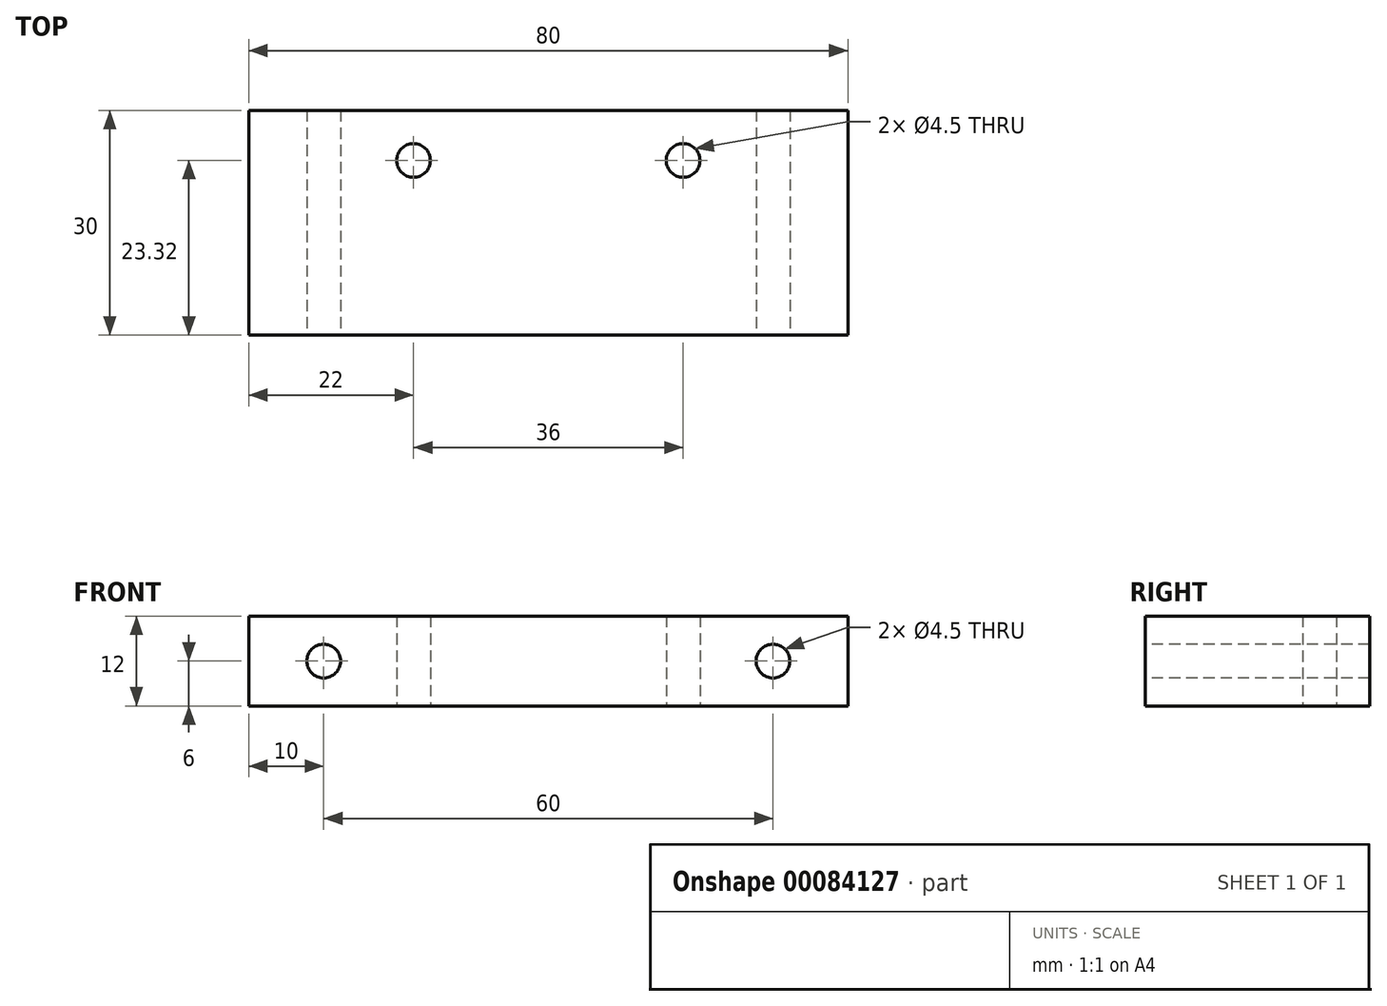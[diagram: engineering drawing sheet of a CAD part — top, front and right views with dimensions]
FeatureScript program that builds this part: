
annotation { "Feature Type Name" : "Feature", "Feature Type Description" : "" }
export const myFeature = defineFeature(function(context is Context, id is Id, definition is map)
    precondition{}
    {
        {
            var Q0;
            Q0=qCreatedBy(makeId("Top.planeOp"),FACE);
            var sketch = newSketch(context, id + "F0", { "sketchPlane" : qUnion([Q0])});
            skLineSegment(sketch, "E0.bottom", {"start": v(40, -15) * mm, "end": v(-40, -15) * mm});
            skLineSegment(sketch, "E0.top", {"start": v(40, 15) * mm, "end": v(-40, 15) * mm});
            skLineSegment(sketch, "E0.left", {"start": v(40, -15) * mm, "end": v(40, 15) * mm});
            skLineSegment(sketch, "E0.right", {"start": v(-40, -15) * mm, "end": v(-40, 15) * mm});
            skPoint(sketch, "E0.middle", {"position": v(0, 0) * mm});
            skLineSegment(sketch, "E1", {"start": v(-18, 8.32) * mm, "end": v(18, 8.32) * mm, "construction": true});
            skPoint(sketch, "E2", {"position": v(0, 8.32) * mm});
            skCircle(sketch, "E3", {"center": v(-18, 8.32) * mm, "radius": 2.25 * mm});
            skCircle(sketch, "E4", {"center": v(18, 8.32) * mm, "radius": 2.25 * mm});
            skSolve(sketch);
        }
        {
            var Q0;
            Q0=makeQuery(id+"F0.imprint","IMPRINT",FACE,{"disambiguationData":[TD([[makeQuery(id+"F0.imprint","IMPRINT",EDGE,{"derivedFrom":sQuery(id+"F0.wireOp",EDGE,"E0.bottom")}),-1.0]])]});
            extrude(context, id + "F1", {"entities" : qUnion([Q0]), "depth" : 12 * mm});
        }
        {
            var Q0;
            Q0=makeQuery(id+"F1.opExtrude","SWEPT_FACE",FACE,{"disambiguationData":[OSD([sQuery(id+"F0.wireOp",EDGE,"E0.bottom")])]});
            var sketch = newSketch(context, id + "F2", { "sketchPlane" : qUnion([Q0])});
            skLineSegment(sketch, "E5", {"start": v(-40, 6) * mm, "end": v(40, 6) * mm, "construction": true});
            skPoint(sketch, "E6", {"position": v(0, 6) * mm});
            skPoint(sketch, "E7", {"position": v(-30, 6) * mm});
            skPoint(sketch, "E8", {"position": v(30, 6) * mm});
            skCircle(sketch, "E9", {"center": v(-30, 6) * mm, "radius": 2.25 * mm});
            skCircle(sketch, "E10", {"center": v(30, 6) * mm, "radius": 2.25 * mm});
            skSolve(sketch);
        }
        {
            var Q0;
            Q0=makeQuery(id+"F2.imprint","IMPRINT",FACE,{"disambiguationData":[TD([[makeQuery(id+"F2.imprint","IMPRINT",EDGE,{"derivedFrom":sQuery(id+"F2.wireOp",EDGE,"E9")}),1.0]])]});
            var Q1;
            Q1=makeQuery(id+"F2.imprint","IMPRINT",FACE,{"disambiguationData":[TD([[makeQuery(id+"F2.imprint","IMPRINT",EDGE,{"derivedFrom":sQuery(id+"F2.wireOp",EDGE,"E10")}),1.0]])]});
            extrude(context, id + "F3", {"entities" : qUnion([Q0, Q1]), "operationType" : NewBodyOperationType.REMOVE, "endBound" : BoundingType.THROUGH_ALL, "oppositeDirection" : true, "depth" : 25 * mm});
        }
    });
